# Revit family: O3EIF
name_source: partatom
category: Mechanical Equipment
units: mm (PartAtom-declared; Revit-internal decimal feet)

## family parameters
Always vertical = Yes
Cut with Voids When Loaded = No
OmniClass Number = 23.40.40.11.17
OmniClass Title = Refrigerated Cases
Part Type = Normal
Room Calculation Point = No
Round Connector Dimension = Use Radius
Shared = No
Work Plane-Based = Yes

## types (2) — shared parameters
ANTI SWEAT APPARENT LOAD = 0 VA
ANTI SWEAT HEATER AMPS = 0 A
ANTI SWEAT HEATER WATTAGE = 0 W
BASE HEIGHT = 10"
BTU ADD FOR LIGHTS = 1680
BTU ADD PER SHELF PER FOOT = 80
BTU PER FOOT CONVENTIONAL = 2836
BTU PER FOOT PARALLEL = 2600
CERTIFICATIONS = NSF 7, UL471, CSA
COIL REFRIGERATION CHARGE = 0.00 lb
CONTROL TYPE = T-STAT
CONVENTIONAL EVAPORATOR LOAD = 21532
DATE = 05/22/12
DEDICATED CIRCUIT = YES
DEFROST AMPS = 0 A
DEFROST PHASE = 1
DEFROST TIME AND DURATION = 2 @ 60 MIN
DEFROST WATTAGE = 0 W
DIEBOARD HEIGHT = 0"
DISCHARGE AIR TEMPERATURE = 30 °F
DRAIN LINE CONNECTION = Drain Connection
DRAIN LINE DIAMETER = 2"
DRAIN LINE RADIUS = 1"
DRAIN PIPE LENGTH = 0"
DRAIN PIPE TYPE = PVC
DRIP PAN PLUMB TYPE = HARD
Default Elevation = 48"
Description = Multi-Deck Island End Cap Merchandiser
ELECTRIC DEFROST = No
ELECTRICAL DEFROST VOLTAGE = 0 V
EQUIPMENT MARK = O3EIF
EVAPORATOR TEMPERATURE = 22 °F
FAN AMPS = 0 A
FAN AND ANTI SWEAT HEATER APPARENT LOAD = 36 VA
FAN APPARENT LOAD = 36 VA
FAN CONNECTOR DESCRIPTION = FAN AND ANTI SWEAT CONNECTOR
FAN NUMBER OF POLES = 1
FAN QUANTITY = 2
FAN TYPE = ECM
FAN WATTAGE = 21 W
GROUND FAULT PROTECTION = NO
HEIGHT = 52 1/8"
HOT GAS DEFROST = No
ISOLATED GROUND REQUIRED = NO
Keynote = Deli / Meat
LED LIGHTING AMPS = 0 A
LED LIGHTING AMPS PER ROW = 0 A
LED LIGHTING BTU ADD PER ROW = 36
LED LIGHTING WATTAGE = 29 W
LEGEND NUMBER = O3EIF
LENGTH = 84 5/16"
LENGTH FOR BTU = 7
LIGHT AMPS = 1 A
LIGHT TYPE = T8 FLUORESCENT
LIGHTING APPARENT LOAD = 101 VA
LIGHTING CONNECTION DESCRIPTION = LIGHTING CONNECTOR
LIGHTING NUMBER OF POLES = 1
LIGHTING WATTAGE = 101 VA
LIQUID LINE CONNECTION = LIQUID LINE CONNECTION
LIQUID LINE DIAMETER = 0"
LIQUID LINE RADIUS = 0"
Manufacturer = HILL PHOENIX
Model = O3EIF
NUMBER OF WIRES = 3
PARALLEL EVAPORATOR LOAD = 19880
PHASE = 1
POWER FACTOR = 1
PRESSURE REGULATOR = 0.00 psi
RECEPTICAL MOUNTING HEIGHT ABOVE FLOOR = 19 3/4"
REF PLANE FRONT BACK = 21 3/16"
REF PLANE LEFT RIGHT = 42 3/16"
REVERSE AIR DEFROST = No
SET BACK MODE FOR ENERGY CONSERVATION = NO
SHELF LIGHT ROWS = 3
SIZE OF COLD WATER HOOK UP = 0"
SIZE OF HOT WATER HOOK-UP = 0"
SUCTION LINE CONNECTION = SUCTION LINE CONNECTION
SUCTION LINE DIAMETER = 1"
SUCTION LINE RADIUS = 0"
T8 LIGHT OR LED LIGHT = Yes
T8 LIGHTING AMPS = 1 A
T8 LIGHTING AMPS PER ROW = 0 A
T8 LIGHTING BTU ADD PER ROW = 80
T8 LIGHTING WATTAGE = 101 W
TIME OFF DEFROST = Yes
TOEKICK HEIGHT = 5 1/2"
TOEKICK INSET = 1 1/2"
TOTAL APPARENT FAN-LIGHT AND A/S LOAD = 122 VA
TOTAL CASE AMPS = 1 A
TOTAL CASE WATTAGE = 122 W
URL = http://www.hillphoenix.com
VOLTAGE = 120 V
WATER LINE MOUNTING HEIGHT ABOVE FLOOR = 0"
WEIGHT = 0.00 lb
WIDTH = 42 3/8"
zero-valued in all types: CORNICE AND NOSE LIGHT ROWS

## type names (no varying parameters)
- O3EIF
- o3eif 2 for schedule use

## geometry (parser evidence)
native form markers: Blend x2, Sweep x6
no freeform markers — native parametric forms only
